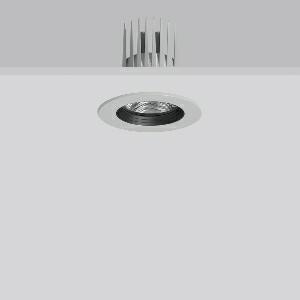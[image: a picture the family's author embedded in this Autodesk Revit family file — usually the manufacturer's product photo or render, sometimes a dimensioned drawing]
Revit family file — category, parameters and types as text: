
# Revit family: heledon_mini_e_901748_004_fd59
name_source: partatom
category: Lighting Fixtures
units: mm (PartAtom-declared; Revit-internal decimal feet)

## family parameters
Cut with Voids When Loaded = No
Host = Face
Light Source = No
Part Type = Normal
Room Calculation Point = No
Round Connector Dimension = Use Diameter
Shared = No

## types (1)
- HELEDON mini E (1 x LED Modul 930, 3550 lm, 3000)
    Apparent Load = 29 VA
    Approval mark = CE
    CIE Flux Codes = 100 100 100 100 100
    Color Rendering = 90
    Color Temperature = 3000
    Default Elevation = 1800 mm
    Description = Series: HELEDON mini
Round recessed downlight. Housing: die-cast aluminium, powder-coated. Black plastic ring and recessed LED to prevent glare from the side. Optical assembly with reflector made of MIRO-Silver with 98% total light reflection for outstanding efficiency - can be changed without tools. Best colour rendering index Ra>90. Suitable for Recessed ceiling mounting. Installation without tools thanks to spring fastening system. Including separate LED converter with connecting cable 600 mm.High quality converter without flickering and stroboscopic effect. Through-wiring box (5 pole) available as accessory. The following accessories can be mounted without use of tools: interchangeable lenses, decorative glasses, honeycomb louvre, clear and frosted diffusers, white interchangeable plastic ring. 
Colour: silver
Diameter: 124 mm
Height: 3 mm
Cut-out diameter: 114 mm
Recess height: 170 mm
Luminaire: recess height: 120 mm
Lamp: LED
Socket: without socket
Colour temperature: 3000K
Colour rendering index (CRI): 92
System power: 29 W
Rated luminous flux: 3550 lm
Luminous efficiency: 122 lm/W
Control gear: Regulated power supply
Protection class: II
Type of protection: IP 20
    Height = 0 mm  [stored 0 ft]
    Lamp = 1 x LED Modul 930
    Lamp Light Flux = 3550 lm
    Lamp count = 1
    Length = 124 mm  [stored 0.406824 ft]
    Lifetime = 50000 h
    Luminous efficacy = 122 lm/W
    Manufacturer = RZB
    ModVariant = No
    Model = 901748.004
    Mounting Place = Ceiling
    Mounting Type = Recessed
    Number of Poles = 1
    OnlyDefault = Yes
    Power Factor = 1
    Product Name = HELEDON mini E
    Product group = Recessed downlights
    ProductGroupID = 402
    Protection Class = Protection class II
    Protection Degree = IP 20
    RLX_Detail_Level = 1
    RLX_Emergency_Light_Flux = 0 lm
    RLX_Emergency_Type = 0
    RLX_Emergency_Type_DB = No
    RlxData = <blob elided: 129045 chars, md5=97ef68f9>
    Socket = socket
    Standby Power = 0 W
    System Light Flux = 3550 lm
    System Power = 29 W
    Type Comments = Product without accessories
    Type Image = 901657.004.jpg
    URL = http://relux.com
    VarID = ---
    Voltage = 230 V
    Voltage Range = 220-240 V
    Weight = 0.00 kg
    Width = 0 mm  [stored 0 ft]

note: [stored X ft] marks values corroborated as IEEE doubles in the binary element streams (Revit-internal decimal feet)

## geometry (parser evidence)
native form markers: Blend x4, Sweep x11
no freeform markers — native parametric forms only
